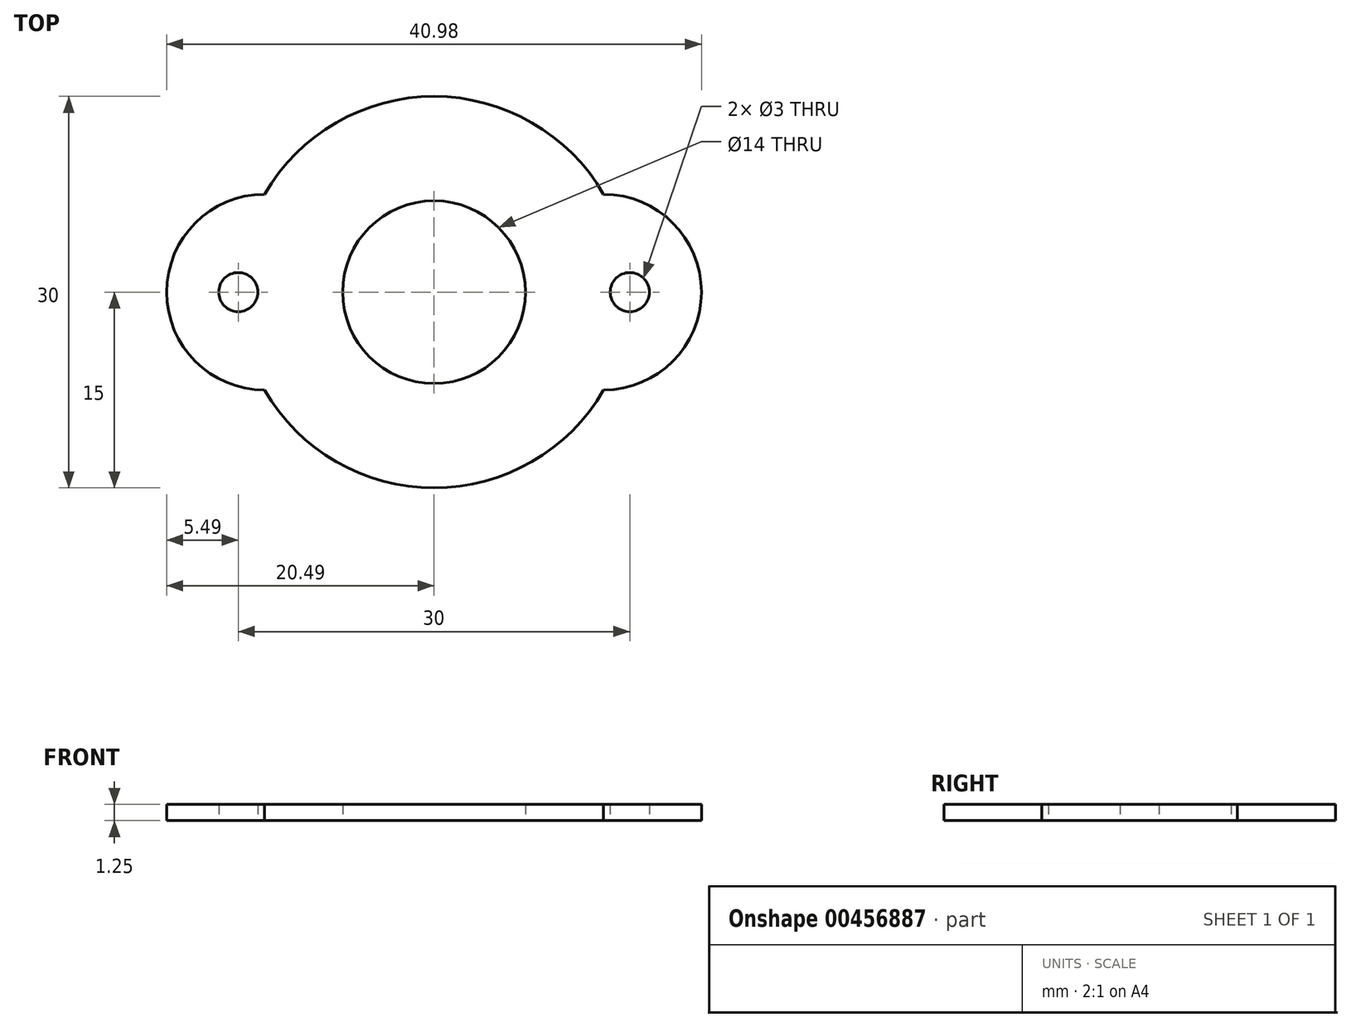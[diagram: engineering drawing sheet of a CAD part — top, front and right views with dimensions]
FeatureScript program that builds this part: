
annotation { "Feature Type Name" : "Feature", "Feature Type Description" : "" }
export const myFeature = defineFeature(function(context is Context, id is Id, definition is map)
    precondition{}
    {
        {
            var Q0;
            Q0=qCreatedBy(makeId("Top.planeOp"),FACE);
            var sketch = newSketch(context, id + "F0", { "sketchPlane" : qUnion([Q0])});
            skCircle(sketch, "E0", {"center": v(0, 0) * mm, "radius": 7 * mm});
            skCircle(sketch, "E1", {"center": v(0, 0) * mm, "radius": 15 * mm});
            skLineSegment(sketch, "E2", {"start": v(13, 7.5) * mm, "end": v(20.5, 7.5) * mm});
            skLineSegment(sketch, "E3", {"start": v(20.5, 7.5) * mm, "end": v(20.5, -7.5) * mm});
            skLineSegment(sketch, "E4", {"start": v(20.5, -7.5) * mm, "end": v(13, -7.5) * mm});
            skLineSegment(sketch, "E5", {"start": v(-13, -7.5) * mm, "end": v(-20.5, -7.5) * mm});
            skLineSegment(sketch, "E6", {"start": v(-20.5, -7.5) * mm, "end": v(-20.5, 7.5) * mm});
            skLineSegment(sketch, "E7", {"start": v(-20.5, 7.5) * mm, "end": v(-13, 7.5) * mm});
            skPoint(sketch, "E8", {"position": v(-15, 0) * mm});
            skPoint(sketch, "E9", {"position": v(15, 0) * mm});
            skCircle(sketch, "E10", {"center": v(0, 0) * mm, "radius": 11 * mm, "construction": true});
            skSolve(sketch);
        }
        {
            var Q0;
            {var subQ0=sQuery(id+"F0.wireOp",EDGE,"E5");Q0=makeQuery(id+"F0.imprint","IMPRINT",FACE,{"disambiguationData":[TD([[makeQuery(id+"F0.imprint","IMPRINT",EDGE,{"derivedFrom":subQ0}),-1.0]])]});}
            var Q1;
            Q1=makeQuery(id+"F0.imprint","IMPRINT",FACE,{"disambiguationData":[TD([[makeQuery(id+"F0.imprint","IMPRINT",EDGE,{"derivedFrom":sQuery(id+"F0.wireOp",EDGE,"E0")}),-1.0]])]});
            var Q2;
            {var subQ0=sQuery(id+"F0.wireOp",EDGE,"E2");Q2=makeQuery(id+"F0.imprint","IMPRINT",FACE,{"disambiguationData":[TD([[makeQuery(id+"F0.imprint","IMPRINT",EDGE,{"derivedFrom":subQ0}),-1.0]])]});}
            extrude(context, id + "F1", {"entities" : qUnion([Q0, Q1, Q2]), "depth" : 1.25 * mm});
        }
        {
            var Q0;
            Q0=makeQuery(id+"F1.opExtrude","SWEPT_EDGE",EDGE,{"disambiguationData":[OSD([sQuery(id+"F0.wireOp",EDGE,"E6"),sQuery(id+"F0.wireOp",EDGE,"E7")])]});
            var Q1;
            Q1=makeQuery(id+"F1.opExtrude","SWEPT_EDGE",EDGE,{"disambiguationData":[OSD([sQuery(id+"F0.wireOp",EDGE,"E5"),sQuery(id+"F0.wireOp",EDGE,"E6")])]});
            var Q2;
            Q2=makeQuery(id+"F1.opExtrude","SWEPT_EDGE",EDGE,{"disambiguationData":[OSD([sQuery(id+"F0.wireOp",EDGE,"E2"),sQuery(id+"F0.wireOp",EDGE,"E3")])]});
            var Q3;
            Q3=makeQuery(id+"F1.opExtrude","SWEPT_EDGE",EDGE,{"disambiguationData":[OSD([sQuery(id+"F0.wireOp",EDGE,"E3"),sQuery(id+"F0.wireOp",EDGE,"E4")])]});
            fillet(context, id + "F2", {"entities" : qUnion([Q0, Q1, Q2, Q3]), "radius" : 7.5 * mm, "tangentPropagation" : true, "allowEdgeOverflow" : false});
        }
        {
            var Q0;
            Q0=sQuery(id+"F0.wireOp",VERTEX,"E9");
            var Q1;
            Q1=sQuery(id+"F0.wireOp",VERTEX,"E8");
            var Q2;
            Q2=makeQuery(id+"F1.opExtrude","SWEPT_BODY",BODY,{"disambiguationData":[OSD([sQuery(id+"F0.wireOp",EDGE,"E0"),sQuery(id+"F0.wireOp",EDGE,"E1"),sQuery(id+"F0.wireOp",EDGE,"E2"),sQuery(id+"F0.wireOp",EDGE,"E3"),sQuery(id+"F0.wireOp",EDGE,"E4"),sQuery(id+"F0.wireOp",EDGE,"E5"),sQuery(id+"F0.wireOp",EDGE,"E6"),sQuery(id+"F0.wireOp",EDGE,"E7")])]});
            hole(context, id + "F3", {"style" : HoleStyle.SIMPLE, "endStyle" : HoleEndStyle.THROUGH, "oppositeDirection" : true, "holeDiameter" : 3 * mm, "isTappedThrough" : true, "tappedDepth" : 12 * mm, "tapClearance" : 3, "locations" : qUnion([Q0, Q1]), "scope" : qUnion([Q2])});
        }
    });
